# Revit family: WC-Close Coupled-Stylus Venecia Suite1
name_source: partatom
category: Plumbing Fixtures
revit_build: Autodesk Revit Architecture 2012 (Build: 20110916_2132(x64)
units: mm (PartAtom-declared; Revit-internal decimal feet)

## types (2) — shared parameters
Assembly Code = C1030210
CW Connection = Yes
Cost = 405.1 $
Description = Venecia Vitreous China Close Coupled 4.5/3L Smartflush Suite
HW Connection = No
Hardware = Metal-Chrome-Caroma
Keynote = WC
Manufacturer = Stylus
Material_ANZRS = Porcelain-White-Caroma
PlumbingMaterial_ANZRS = Porcelain-White-Caroma
URL = www.stylus.com.au
Vent Connection = No
WELSRating_ANZRS = 4
Waste Connection = Yes
zero-valued in all types: Default Elevation

## per-type parameters (varying)
| type | Model | Type Comments |
| S Trap | W45004VP | Venecia 4.5/3L Smartflush Close Coupled Toilet Suite |
| P Trap | W45001VP | Venecia 6/3L Smartflush Close Coupled Toilet Suite |

## geometry (parser evidence)
native form markers: Blend x8, Sweep x3
no freeform markers — native parametric forms only
